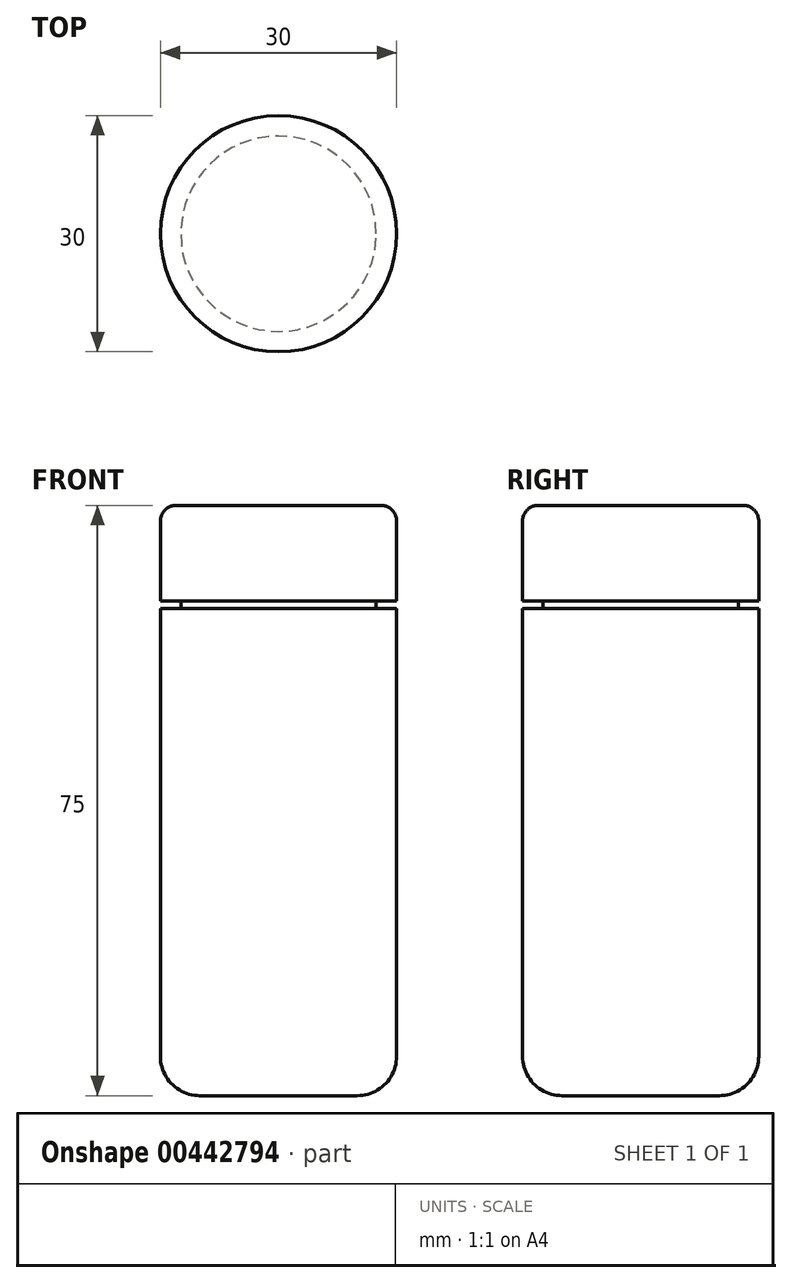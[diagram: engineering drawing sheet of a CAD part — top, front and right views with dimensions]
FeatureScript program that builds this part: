
annotation { "Feature Type Name" : "Feature", "Feature Type Description" : "" }
export const myFeature = defineFeature(function(context is Context, id is Id, definition is map)
    precondition{}
    {
        {
            var Q0;
            Q0=qCreatedBy(makeId("Top.planeOp"),FACE);
            var sketch = newSketch(context, id + "F0", { "sketchPlane" : qUnion([Q0])});
            skCircle(sketch, "E0", {"center": v(0, 0) * mm, "radius": 15 * mm});
            skSolve(sketch);
        }
        {
            var Q0;
            Q0 = qSketchRegion(id + "F0", true);
            extrude(context, id + "F1", {"entities" : qUnion([Q0]), "depth" : 75 * mm});
        }
        {
            var Q0;
            Q0=makeQuery(id+"F1.opExtrude","CAP_EDGE",EDGE,{"disambiguationData":[OSD([sQuery(id+"F0.wireOp",EDGE,"E0")])],"isStart":true});
            fillet(context, id + "F2", {"entities" : qUnion([Q0]), "radius" : 5 * mm, "tangentPropagation" : true, "allowEdgeOverflow" : false});
        }
        {
            var Q0;
            Q0=makeQuery(id+"F1.opExtrude","CAP_EDGE",EDGE,{"disambiguationData":[OSD([sQuery(id+"F0.wireOp",EDGE,"E0")])],"isStart":false});
            fillet(context, id + "F3", {"entities" : qUnion([Q0]), "radius" : 2 * mm, "tangentPropagation" : true, "allowEdgeOverflow" : false});
        }
        {
            var Q0;
            Q0=qCreatedBy(makeId("Right.planeOp"),FACE);
            var sketch = newSketch(context, id + "F4", { "sketchPlane" : qUnion([Q0])});
            skLineSegment(sketch, "E1.bottom", {"start": v(19.34, 62.86) * mm, "end": v(12.41, 62.86) * mm});
            skLineSegment(sketch, "E1.top", {"start": v(19.34, 61.86) * mm, "end": v(12.41, 61.86) * mm});
            skLineSegment(sketch, "E1.left", {"start": v(19.34, 62.86) * mm, "end": v(19.34, 61.86) * mm});
            skLineSegment(sketch, "E1.right", {"start": v(12.41, 62.86) * mm, "end": v(12.41, 61.86) * mm});
            skLineSegment(sketch, "E2", {"start": v(0, 0) * mm, "end": v(0, 110.33) * mm, "construction": true});
            skSolve(sketch);
        }
        {
            var Q0;
            Q0 = qSketchRegion(id + "F4", true);
            var Q1;
            Q1=sQuery(id+"F4.wireOp",EDGE,"E2");
            var Q2;
            Q2=sQuery(id+"F4.wireOp",EDGE,"E2");
            revolve(context, id + "F5", {"operationType" : NewBodyOperationType.REMOVE, "entities" : qUnion([Q0]), "surfaceEntities" : qUnion([Q1]), "axis" : qUnion([Q2]), "revolveType" : RevolveType.FULL, "oppositeDirection" : true});
        }
    });
